# Revit family: IS_i-lifeS_E2112_BIM_GB
name_source: partatom
category: Plumbing Fixtures
units: mm (PartAtom-declared; Revit-internal decimal feet)

## family parameters
Always vertical = No
Cut with Voids When Loaded = No
OmniClass Number = 23.45.05.14.14
OmniClass Title = Sinks/Lavatories
Part Type = Normal
Room Calculation Point = No
Round Connector Dimension = Use Diameter
Shared = No
Work Plane-Based = No

## types (3) — shared parameters
Accessories = https://www.idealstandard.co.uk
AreaUnits = Millimetres
BIMObjectName = IS_IdealStandard_Wall-HungHandRinseBasins_i.life_E2112
BIMobject category = Wash Basins
BIMobject category code = wash-basins
BIMobject main category = Sanitary
BIMobject main category code = sanitary
Brand = Ideal Standard
Brand url = https://www.idealstandard.co.uk
Category = Sanitary
Classification = Basin
ConnectionType = plumbing
CurrencyUnit = £
CurrentRevision = 1
Date of publishing = 14/11/2022
Description = i.life S 37cm guest washbasin, 1 taphole, no overflow, right hand
DurationUnit = years
Edition number = 1
ElementType = Fixed
ExpectedLife = 99
Features = 37cm guest washbasin, 1 taphole, no overflow, right hand
Help = https://www.idealstandard.co.uk
IFC Classification = Sanitary Terminal
IfcExportAs = IfcSanitaryTerminalType
IfcExportType = WASHHANDBASIN
Installation instructions = https://www.idealstandard.co.uk
InstallationInstructions = https://www.idealstandard.co.uk
LinearUnits = Millimetres
MaintenanceInformation = https://www.idealstandard.co.uk
Manufacturer = Ideal Standard
Manufacturer name = Ideal standard test account
ManufacturerURL = https://www.idealstandard.co.uk
Material = Ceramics
Material main = Ceramics
NBS Reference Code = 45-35-70/369
NBS Reference Description = Wall hung wash basins
Name = Wall-HungHandRinseBasins_i.life_E2112_IdealStandard
NettWeight = 6.2
NominalDepth = 210 mm
NominalHeight = 120 mm
NominalLength = 210 mm
NominalWidth = 370 mm
OmniClass Code = 23-39 29 13 21 19
OmniClass Description = Surface Water Retencion Basins
PredefinedType = Sanitary
Product Guid = 854d4f07-95af-4f5e-aa18-78e112e4a9ad
Product SKU = E2112
Product certification = https://www.idealstandard.co.uk
Product data url = https://www.idealstandard.co.uk
Product family = i.life
Product group = Plumbing Fixtures
Product name = TEMPO/EUROVIT H/R BSN 37X21 WHT NOF BXD
Product url = https://www.idealstandard.co.uk
ProductInformation = https://www.idealstandard.co.uk
Shape = Sculpture
Size = 370 x 210 x 120 mm
Space = Internal
SpareParts = https://www.idealstandard.co.uk
Technical description = https://www.idealstandard.co.uk
UNSPSC Code = 301815
URL = https://www.idealstandard.co.uk
Uniclass 1.4 Code = L7212
Uniclass 1.4 Description = Washbasin
Uniclass 2.0 Code = Pr_40_30_79_95
Uniclass 2.0 Description = Wall-Hung Hand Rinse Basins
Uniclass 2015 Code = Pr_40_20_96_96
Uniclass 2015 Name = Wall-hung washbasins
Uniclass2015Code = Pr_40_20_96_96
Uniclass2015Title = Wall-hung washbasins
Uniclass2015Version = v1.27
Uniformat II Code = D2010
Uniformat II Description = Plumbing Fixtures
Version = 1
VolumeUnits = litres
WRASURL = https://www.wrasapprovals.co.uk
WarrantyDescription = manufacturer warranty
WarrantyDurationUnit = years
Weight Net (Kg) = 6.2
Youtube clip = https://www.youtube.com

## per-type parameters (varying)
| type | BarCode | Color | Finish | GTIN code | MainColor | Model | ModelNumber |
| E2112V3 - i.life S 37cm Vessel Washbasin - Silk Black | 5017830556855 | Silk Black | Silk Black | https://5017830556855 | Silk Balck | E2112V3 | E2112V3 |
| E2112V1 - i.life S 37cm Vessel Washbasin - Silk White | 5017830556848 | Silk White | Silk White | https://5017830556848 | Silk White | E2112V1 | E2112V1 |
| E211201 - i.life S 37cm Vessel Washbasin - White | 5017830543923 | white | White | https://5017830543923 | White | E211201 | E211201 |

note: column(s) folded — value = type name in every type: ModelReference

## geometry (parser evidence)
native form markers: Sweep x2
no freeform markers — native parametric forms only
